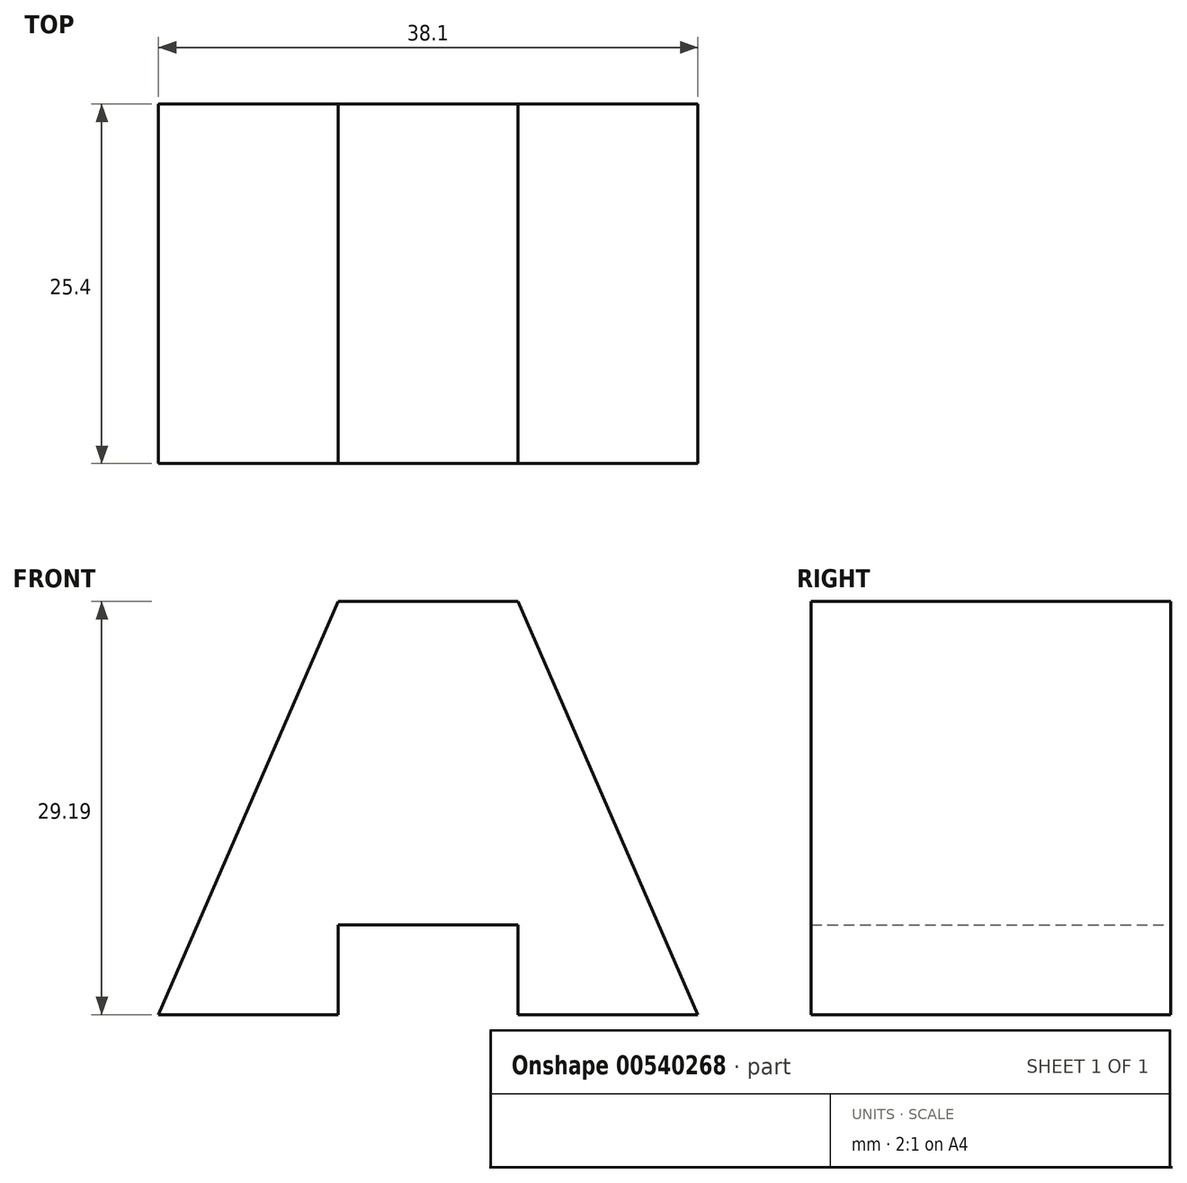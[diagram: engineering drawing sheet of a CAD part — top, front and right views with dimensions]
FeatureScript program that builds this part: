
annotation { "Feature Type Name" : "Feature", "Feature Type Description" : "" }
export const myFeature = defineFeature(function(context is Context, id is Id, definition is map)
    precondition{}
    {
        {
            var Q0;
            Q0=qCreatedBy(makeId("Front.planeOp"),FACE);
            var sketch = newSketch(context, id + "F0", { "sketchPlane" : qUnion([Q0])});
            skLineSegment(sketch, "E0", {"start": v(-34.94, 29.19) * mm, "end": v(-47.64, 29.19) * mm});
            skLineSegment(sketch, "E1", {"start": v(-47.64, 29.19) * mm, "end": v(-60.34, 0) * mm});
            skLineSegment(sketch, "E2", {"start": v(-60.34, 0) * mm, "end": v(-47.64, 0) * mm});
            skLineSegment(sketch, "E3", {"start": v(-47.64, 0) * mm, "end": v(-47.64, 6.35) * mm});
            skLineSegment(sketch, "E4", {"start": v(-34.94, 29.19) * mm, "end": v(-22.24, 0) * mm});
            skLineSegment(sketch, "E5", {"start": v(-22.24, 0) * mm, "end": v(-34.94, 0) * mm});
            skLineSegment(sketch, "E6", {"start": v(-34.94, 0) * mm, "end": v(-34.94, 6.35) * mm});
            skLineSegment(sketch, "E7", {"start": v(-34.94, 6.35) * mm, "end": v(-47.64, 6.35) * mm});
            skSolve(sketch);
        }
        {
            var Q0;
            Q0 = qSketchRegion(id + "F0", true);
            extrude(context, id + "F1", {"entities" : qUnion([Q0]), "depth" : 25.4 * mm, "offsetDistance" : 25.4 * mm});
        }
    });
